# Revit family: OglaendSystem_FOE_SpliceConnector_82L
name_source: partatom
category: Соединительные детали кабельных лотков
revit_build: Autodesk Revit 2018 (Build: 20170927_1515(x64)
units: mm (PartAtom-declared; Revit-internal decimal feet)

## family parameters
Всегда вертикально = Нет
Заголовок OmniClass = Cable Trays and Horizontal Racks
На основе рабочей плоскости = Да
Номер OmniClass = 23.80.30.17.17
Общий = Да
При загрузке вырезать с полостями = Нет
Размер круглого соединителя = Использовать диаметр
Тип детали = Мультипорт канального

## types (2) — shared parameters
Отметка по умолчанию = 1219.2 мм
Рзм.X = 220 мм

## per-type parameters (varying)
| type | Таблица выбора артикула | Таблица выбора массы | Таблица выбора наименования | Таблица выбора типа |
| Исполнение SS. | FOE SC SS A | FOE SC SS W | FOE SC SS N | FOE SC SS T |
| Исполнение FRP. | FOE SC FRP A | FOE SC FRP W | FOE SC FRP N | FOE SC FRP T |

## geometry (parser evidence)
native form markers: Blend x2
no freeform markers — native parametric forms only
